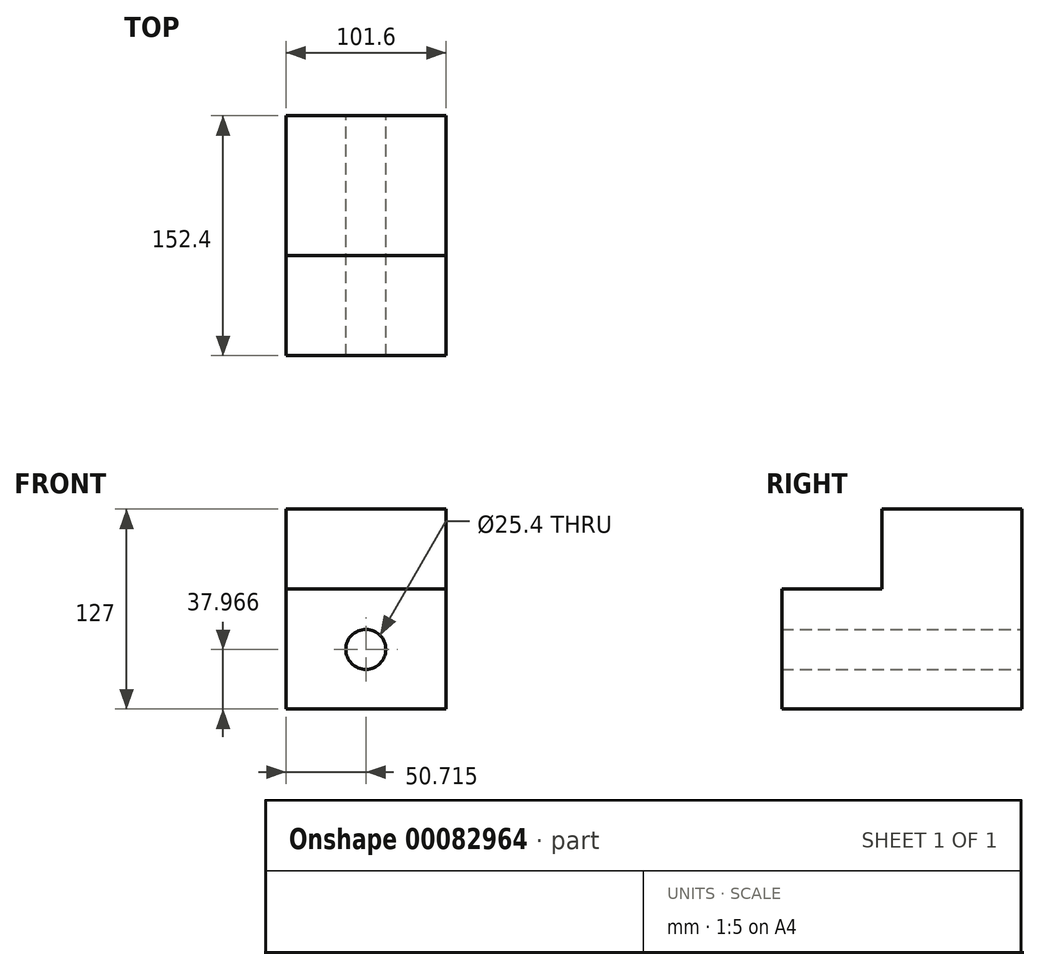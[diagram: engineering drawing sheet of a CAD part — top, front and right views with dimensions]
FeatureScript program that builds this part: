
annotation { "Feature Type Name" : "Feature", "Feature Type Description" : "" }
export const myFeature = defineFeature(function(context is Context, id is Id, definition is map)
    precondition{}
    {
        {
            var Q0;
            Q0=qCreatedBy(makeId("Top.planeOp"),FACE);
            var sketch = newSketch(context, id + "F0", { "sketchPlane" : qUnion([Q0])});
            skLineSegment(sketch, "E0.bottom", {"start": v(-57.14, 105.44) * mm, "end": v(44.46, 105.44) * mm});
            skLineSegment(sketch, "E0.top", {"start": v(-57.14, -46.96) * mm, "end": v(44.46, -46.96) * mm});
            skLineSegment(sketch, "E0.left", {"start": v(-57.14, 105.44) * mm, "end": v(-57.14, -46.96) * mm});
            skLineSegment(sketch, "E0.right", {"start": v(44.46, 105.44) * mm, "end": v(44.46, -46.96) * mm});
            skSolve(sketch);
        }
        {
            var Q0;
            Q0=makeQuery(id+"F0.imprint","IMPRINT",FACE,{"disambiguationData":[TD([[makeQuery(id+"F0.imprint","IMPRINT",EDGE,{"derivedFrom":sQuery(id+"F0.wireOp",EDGE,"E0.bottom")}),-1.0]])]});
            extrude(context, id + "F1", {"entities" : qUnion([Q0]), "depth" : 127 * mm});
        }
        {
            var Q0;
            Q0=makeQuery(id+"F1.opExtrude","SWEPT_FACE",FACE,{"disambiguationData":[OSD([sQuery(id+"F0.wireOp",EDGE,"E0.left")])]});
            var sketch = newSketch(context, id + "F2", { "sketchPlane" : qUnion([Q0])});
            skLineSegment(sketch, "E1.bottom", {"start": v(46.96, 127) * mm, "end": v(-16.54, 127) * mm});
            skLineSegment(sketch, "E1.top", {"start": v(46.96, 76.2) * mm, "end": v(-16.54, 76.2) * mm});
            skLineSegment(sketch, "E1.left", {"start": v(46.96, 127) * mm, "end": v(46.96, 76.2) * mm});
            skLineSegment(sketch, "E1.right", {"start": v(-16.54, 127) * mm, "end": v(-16.54, 76.2) * mm});
            skSolve(sketch);
        }
        {
            var Q0;
            Q0 = qSketchRegion(id + "F2", true);
            extrude(context, id + "F3", {"entities" : qUnion([Q0]), "operationType" : NewBodyOperationType.REMOVE, "endBound" : BoundingType.THROUGH_ALL, "oppositeDirection" : true, "depth" : 127 * mm});
        }
        {
            var Q0;
            Q0=makeQuery(id+"F1.opExtrude","SWEPT_FACE",FACE,{"disambiguationData":[OSD([sQuery(id+"F0.wireOp",EDGE,"E0.bottom")])]});
            var sketch = newSketch(context, id + "F4", { "sketchPlane" : qUnion([Q0])});
            skLineSegment(sketch, "E2.bottom", {"start": v(-44.46, 0) * mm, "end": v(6.34, 0) * mm});
            skLineSegment(sketch, "E2.top", {"start": v(-44.46, 38.1) * mm, "end": v(6.34, 38.1) * mm});
            skLineSegment(sketch, "E2.left", {"start": v(-44.46, 0) * mm, "end": v(-44.46, 38.1) * mm});
            skLineSegment(sketch, "E2.right", {"start": v(6.34, 0) * mm, "end": v(6.34, 38.1) * mm});
            skSolve(sketch);
        }
        {
            var Q0;
            Q0=makeQuery(id+"F4.imprint","IMPRINT",FACE,{"disambiguationData":[TD([[makeQuery(id+"F4.imprint","IMPRINT",EDGE,{"derivedFrom":sQuery(id+"F4.wireOp",EDGE,"E2.bottom")}),-1.0]])]});
            var sketch = newSketch(context, id + "F5", { "sketchPlane" : qUnion([Q0])});
            skCircle(sketch, "E3", {"center": v(6.42, 37.97) * mm, "radius": 12.7 * mm});
            skSolve(sketch);
        }
        {
            var Q0;
            Q0 = qSketchRegion(id + "F5", true);
            extrude(context, id + "F6", {"entities" : qUnion([Q0]), "operationType" : NewBodyOperationType.REMOVE, "endBound" : BoundingType.THROUGH_ALL, "oppositeDirection" : true, "depth" : 25.4 * mm});
        }
    });
